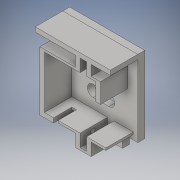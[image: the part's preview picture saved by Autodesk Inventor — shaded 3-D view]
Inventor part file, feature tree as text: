
AUTODESK INVENTOR PART (.ipt)
format: ipt  version: 2016 (Build 200138000, 138)  size: 340,480 bytes
history: native  units: in
note: dims shown in document units (in); Inventor stores cm internally (conversion verified against a paired STEP export)
features: sketch x9, extrude x8, hole x1
ambient origin geometry x8: Origin, YZ Plane, XZ Plane, XY Plane, X Axis, Y Axis, Z Axis, Center Point
bodies: Solid1 (feature_tree)
feature tree (18):
  extrude  "Extrusion1"  Depth=0.1181in
  sketch  "Sketch12"  dims[d11=0.0787in d12=0.0787in d13=0.0787in d14=0.0787in d82=0.9016in d83=0.8858in]
  extrude  "Extrusion7"  Depth=0.0787in
  extrude  "Extrusion12"  Depth=0.1102in
  extrude  "Extrusion13"  Depth=0.6142in
  hole  "Hole4"  [1 undecoded]
  extrude  "Extrusion14"  Depth=0.2165in
  extrude  "Extrusion15"  Depth=0.2165in
  extrude  "Extrusion18"  Depth=0.0787in
  extrude  "Extrusion20"  Depth=0.0787in
  sketch  "Sketch1"  dims[d2=0.1181in d3=0.0in d6=0.8976in d9=0.357in d10=0.7139in]
  sketch  "Sketch22"  dims[d85=0.1102in d86=0.1102in]
  sketch  "Sketch32"  dims[d87=0.6142in d88=0.6142in]
  sketch  "Sketch33"  dims[d89=0.1614in d90=0.1614in]
  sketch  "Sketch35"  dims[d91=0.2992in d92=0.2165in]
  sketch  "Sketch36"  dims[d93=0.2165in d95=0.9016in]
  sketch  "Sketch41"  dims[d97=0.0787in d98=0.0787in]
  sketch  "Sketch43"  dims[d100=0.0787in d101=0.0787in d102=0.0787in d103=0.1693in d105=0.0787in d106=0.0394in d107=0.0394in d108=0.0394in d109=0.0394in d110=0.1575in d111=0.0787in d112=0.0787in d113=0.0394in d114=0.9016in d125=0.1378in d130=0.185in d132=0.3543in d133=0.2165in d139=0.0394in d164=0.3937in d165=0.0in d181=0.0787in d182=0.0787in d185=0.1772in d186=0.0483in d187=0.1063in d188=0.4724in d189=0.0in d190=0.3135in d191=0.4724in d192=0.0in d194=0.2559in d195=0.0394in d196=0.2559in d197=0.0394in d198=0.0787in d199=0.2362in d200=0.1575in d201=0.0787in d202=90.0deg d203=0.315in d204=0.8108in d205=0.1575in d206=0.0in d207=0.0394in d208=0.3937in d209=0.0in d252=0.0197in d253=0.0in d267=0.1969in d268=0.1969in d269=0.1575in d270=0.1575in d271=0.3937in d272=0.0in d26=0.0394in d27=0.0394in d147=0.0394in d148=0.0394in]
note: 1 required parameter value undecoded (feature->parameter linkage not recoverable at this tier; creation-order binding heuristic only, values carry confidence <= 0.55)
